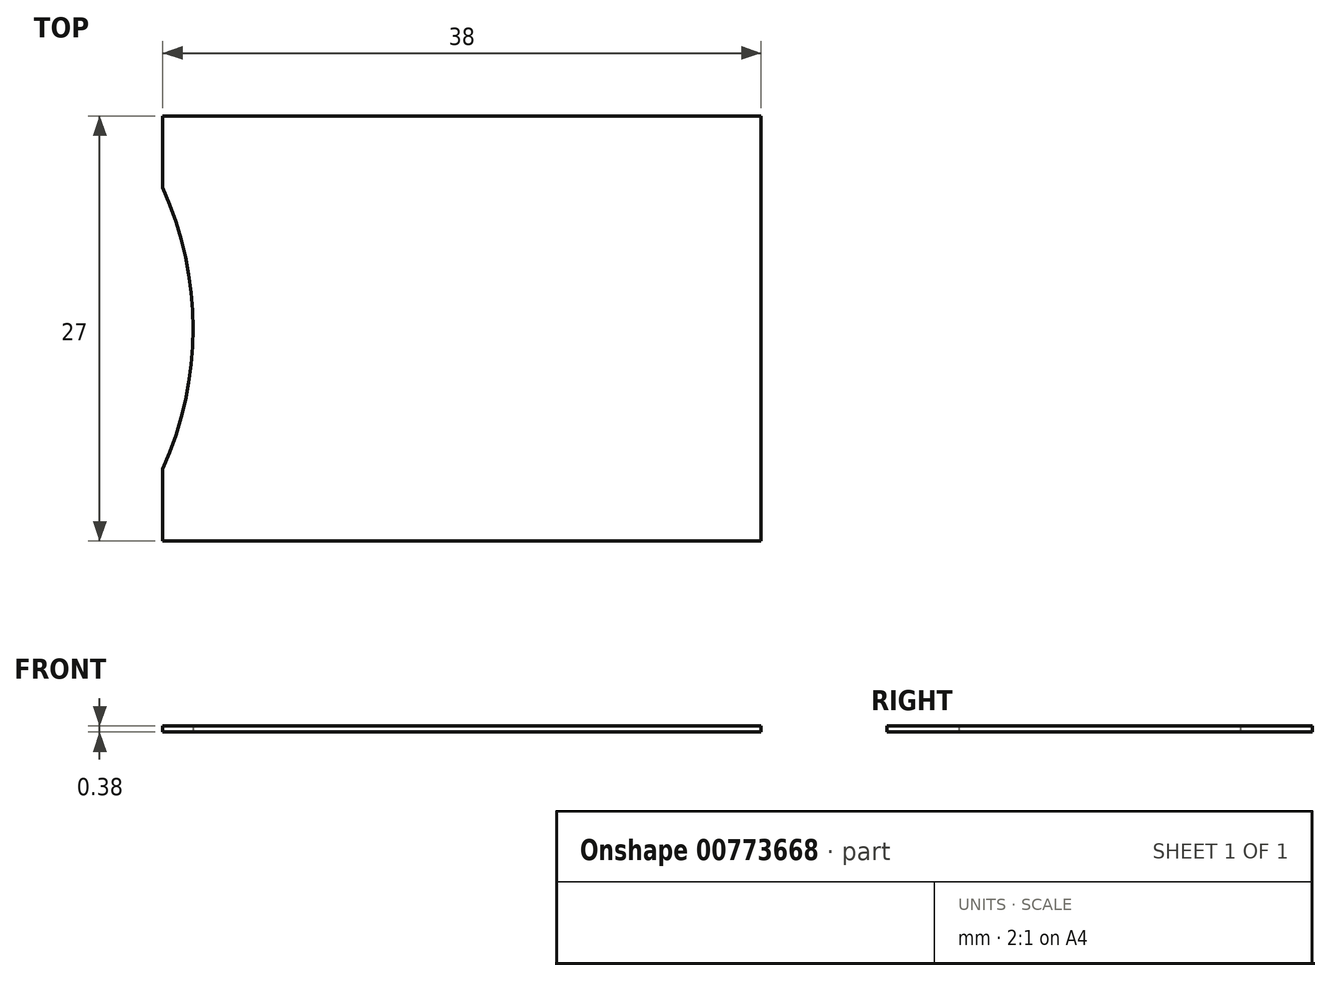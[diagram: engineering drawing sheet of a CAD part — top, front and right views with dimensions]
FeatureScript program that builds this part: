
annotation { "Feature Type Name" : "Feature", "Feature Type Description" : "" }
export const myFeature = defineFeature(function(context is Context, id is Id, definition is map)
    precondition{}
    {
        {
            var Q0;
            Q0=qCreatedBy(makeId("Top.planeOp"),FACE);
            var sketch = newSketch(context, id + "F0", { "sketchPlane" : qUnion([Q0])});
            skLineSegment(sketch, "E0.bottom", {"start": v(0, 0) * mm, "end": v(38, 0) * mm});
            skLineSegment(sketch, "E0.top", {"start": v(0, 27) * mm, "end": v(38, 27) * mm});
            skLineSegment(sketch, "E0.left", {"start": v(0, 0) * mm, "end": v(0, 4.56) * mm});
            skLineSegment(sketch, "E0.right", {"start": v(38, 0) * mm, "end": v(38, 27) * mm});
            skArc(sketch, "E1", {"start": v(0, 22.44) * mm, "mid": v(1.91, 13.5) * mm, "end": v(0, 4.56) * mm});
            skLineSegment(sketch, "E2.trimOffspring", {"start": v(0, 22.44) * mm, "end": v(0, 27) * mm});
            skSolve(sketch);
        }
        {
            var Q0;
            Q0 = qSketchRegion(id + "F0", true);
            extrude(context, id + "F1", {"entities" : qUnion([Q0]), "depth" : 0.38 * mm, "offsetDistance" : 25 * mm});
        }
    });
